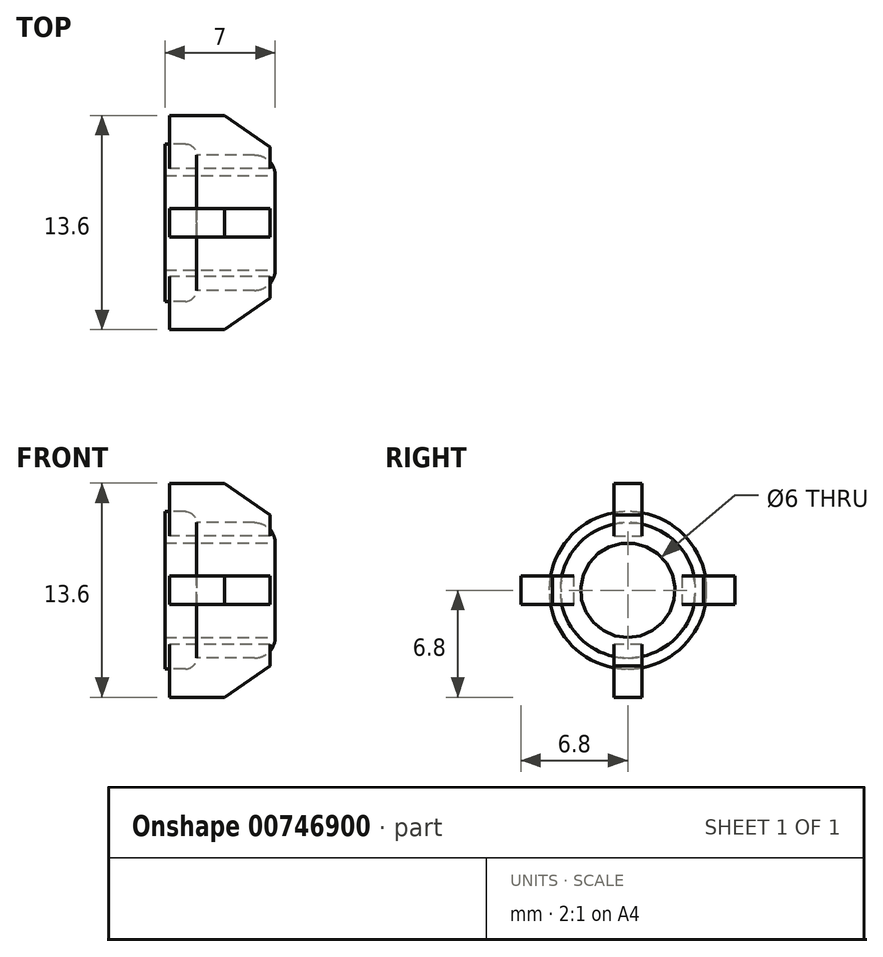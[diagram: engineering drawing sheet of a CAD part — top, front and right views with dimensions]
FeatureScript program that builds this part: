
annotation { "Feature Type Name" : "Feature", "Feature Type Description" : "" }
export const myFeature = defineFeature(function(context is Context, id is Id, definition is map)
    precondition{}
    {
        {
            var Q0;
            Q0=qCreatedBy(makeId("Right.planeOp"),FACE);
            var sketch = newSketch(context, id + "F0", { "sketchPlane" : qUnion([Q0])});
            skCircle(sketch, "E0", {"center": v(0, 0) * mm, "radius": 5 * mm});
            skSolve(sketch);
        }
        {
            var Q0;
            Q0=makeQuery(id+"F0.imprint","IMPRINT",FACE,{"disambiguationData":[TD([[makeQuery(id+"F0.imprint","IMPRINT",EDGE,{"derivedFrom":sQuery(id+"F0.wireOp",EDGE,"E0")}),1.0]])]});
            extrude(context, id + "F1", {"entities" : qUnion([Q0]), "depth" : 2 * mm, "offsetDistance" : 25 * mm});
        }
        {
            var Q0;
            Q0=makeQuery(id+"F1.opExtrude","CAP_FACE",FACE,{"disambiguationData":[OSD([sQuery(id+"F0.wireOp",EDGE,"E0")])],"isStart":false});
            fillet(context, id + "F2", {"entities" : qUnion([Q0]), "radius" : 0.7 * mm, "tangentPropagation" : true, "allowEdgeOverflow" : false});
        }
        {
            var Q0;
            Q0=makeQuery(id+"F1.opExtrude","CAP_FACE",FACE,{"disambiguationData":[OSD([sQuery(id+"F0.wireOp",EDGE,"E0")])],"isStart":false});
            var sketch = newSketch(context, id + "F3", { "sketchPlane" : qUnion([Q0])});
            skCircle(sketch, "E1", {"center": v(0, 0) * mm, "radius": 4.3 * mm});
            skSolve(sketch);
        }
        {
            var Q0;
            Q0 = qSketchRegion(id + "F3", true);
            extrude(context, id + "F4", {"entities" : qUnion([Q0]), "operationType" : NewBodyOperationType.ADD, "depth" : 5 * mm, "offsetDistance" : 25 * mm});
        }
        {
            var Q0;
            Q0=makeQuery(id+"F4.opExtrude","CAP_FACE",FACE,{"disambiguationData":[OSD([sQuery(id+"F3.wireOp",EDGE,"E1")])],"isStart":false});
            fillet(context, id + "F5", {"entities" : qUnion([Q0]), "radius" : 1.3 * mm, "tangentPropagation" : true, "allowEdgeOverflow" : false});
        }
        {
            var Q0;
            Q0=makeQuery(id+"F4.opExtrude","CAP_FACE",FACE,{"disambiguationData":[OSD([sQuery(id+"F3.wireOp",EDGE,"E1")])],"isStart":false});
            var sketch = newSketch(context, id + "F6", { "sketchPlane" : qUnion([Q0])});
            skCircle(sketch, "E2", {"center": v(0, 0) * mm, "radius": 3 * mm});
            skSolve(sketch);
        }
        {
            var Q0;
            Q0 = qSketchRegion(id + "F6", true);
            extrude(context, id + "F7", {"entities" : qUnion([Q0]), "operationType" : NewBodyOperationType.REMOVE, "oppositeDirection" : true, "depth" : 25 * mm, "offsetDistance" : 25 * mm});
        }
        {
            var Q0;
            Q0=qCreatedBy(makeId("Top.planeOp"),FACE);
            var sketch = newSketch(context, id + "F8", { "sketchPlane" : qUnion([Q0])});
            skLineSegment(sketch, "E3", {"start": v(0.28, 4.8) * mm, "end": v(0.28, 6.8) * mm});
            skLineSegment(sketch, "E4", {"start": v(0.28, 6.8) * mm, "end": v(3.78, 6.8) * mm});
            skLineSegment(sketch, "E5", {"start": v(3.78, 6.8) * mm, "end": v(6.68, 4.8) * mm});
            skLineSegment(sketch, "E6", {"start": v(6.68, 3.43) * mm, "end": v(0.28, 3.43) * mm});
            skLineSegment(sketch, "E7", {"start": v(6.68, 3.43) * mm, "end": v(6.68, 4.8) * mm});
            skLineSegment(sketch, "E8", {"start": v(0.28, 3.43) * mm, "end": v(0.28, 4.8) * mm});
            skSolve(sketch);
        }
        {
            var Q0;
            Q0 = qSketchRegion(id + "F8", true);
            extrude(context, id + "F9", {"entities" : qUnion([Q0]), "endBound" : BoundingType.SYMMETRIC, "depth" : 1.8 * mm, "offsetDistance" : 25 * mm});
        }
        {
            var Q0;
            Q0=makeQuery(id+"F9.opExtrude","SWEPT_BODY",BODY,{"disambiguationData":[OSD([sQuery(id+"F8.wireOp",EDGE,"E3"),sQuery(id+"F8.wireOp",EDGE,"E4"),sQuery(id+"F8.wireOp",EDGE,"E5"),sQuery(id+"F8.wireOp",EDGE,"E6"),sQuery(id+"F8.wireOp",EDGE,"E7"),sQuery(id+"F8.wireOp",EDGE,"E8")])]});
            var Q1;
            Q1=makeQuery(id+"F4.opExtrude","SWEPT_FACE",FACE,{"disambiguationData":[OSD([sQuery(id+"F3.wireOp",EDGE,"E1")])]});
            circularPattern(context, id + "F10", {"entities" : qUnion([Q0]), "axis" : qUnion([Q1]), "angle" : 360 * degree, "instanceCount" : 4, "equalSpace" : true});
        }
    });
